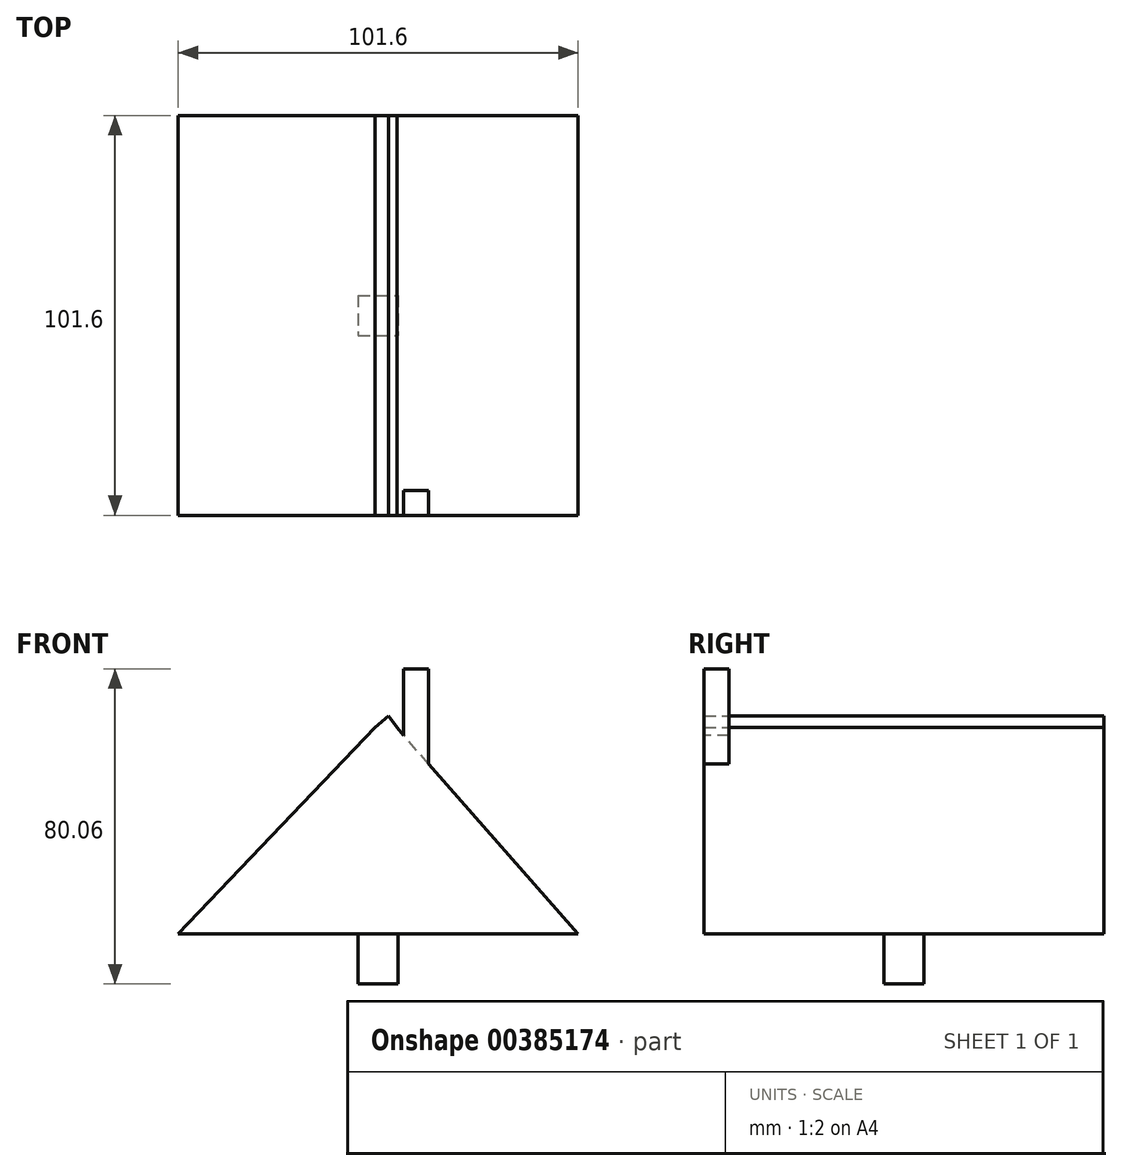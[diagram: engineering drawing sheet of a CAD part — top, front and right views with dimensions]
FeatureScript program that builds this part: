
annotation { "Feature Type Name" : "Feature", "Feature Type Description" : "" }
export const myFeature = defineFeature(function(context is Context, id is Id, definition is map)
    precondition{}
    {
        {
            var Q0;
            Q0=qCreatedBy(makeId("Front.planeOp"),FACE);
            var sketch = newSketch(context, id + "F0", { "sketchPlane" : qUnion([Q0])});
            skLineSegment(sketch, "E0", {"start": v(-53.38, -50.48) * mm, "end": v(48.22, -50.48) * mm});
            skLineSegment(sketch, "E1", {"start": v(-53.38, -50.48) * mm, "end": v(-3.4, 1.96) * mm});
            skLineSegment(sketch, "E2", {"start": v(48.22, -50.48) * mm, "end": v(2.2, 1.96) * mm});
            skLineSegment(sketch, "E3", {"start": v(-3.4, 1.96) * mm, "end": v(0, 4.94) * mm});
            skLineSegment(sketch, "E4", {"start": v(2.2, 1.96) * mm, "end": v(0, 4.94) * mm});
            skSolve(sketch);
        }
        {
            var Q0;
            Q0=makeQuery(id+"F0.imprint","IMPRINT",FACE,{"disambiguationData":[TD([[makeQuery(id+"F0.imprint","IMPRINT",EDGE,{"derivedFrom":sQuery(id+"F0.wireOp",EDGE,"E0")}),1.0]])]});
            extrude(context, id + "F1", {"entities" : qUnion([Q0]), "depth" : 101.6 * mm});
        }
        {
            var Q0;
            Q0=makeQuery(id+"F1.opExtrude","CAP_FACE",FACE,{"disambiguationData":[OSD([sQuery(id+"F0.wireOp",EDGE,"E0"),sQuery(id+"F0.wireOp",EDGE,"E1"),sQuery(id+"F0.wireOp",EDGE,"E2"),sQuery(id+"F0.wireOp",EDGE,"E3"),sQuery(id+"F0.wireOp",EDGE,"E4")])],"isStart":false});
            var sketch = newSketch(context, id + "F2", { "sketchPlane" : qUnion([Q0])});
            skLineSegment(sketch, "E5", {"start": v(3.92, 0) * mm, "end": v(3.92, 16.88) * mm});
            skLineSegment(sketch, "E6", {"start": v(3.92, 16.88) * mm, "end": v(10.27, 16.88) * mm});
            skLineSegment(sketch, "E7", {"start": v(10.27, 16.88) * mm, "end": v(10.27, -7.24) * mm});
            skSolve(sketch);
        }
        {
            var Q0;
            {var subQ0=sQuery(id+"F2.wireOp",EDGE,"E5");Q0=makeQuery(id+"F2.imprint","IMPRINT",FACE,{"disambiguationData":[TD([[makeQuery(id+"F2.imprint","IMPRINT",EDGE,{"derivedFrom":subQ0}),-1.0]])]});}
            extrude(context, id + "F3", {"entities" : qUnion([Q0]), "operationType" : NewBodyOperationType.ADD, "oppositeDirection" : true, "depth" : 6.35 * mm});
        }
        {
            var Q0;
            Q0=makeQuery(id+"F1.opExtrude","SWEPT_FACE",FACE,{"disambiguationData":[OSD([sQuery(id+"F0.wireOp",EDGE,"E0")])]});
            var sketch = newSketch(context, id + "F4", { "sketchPlane" : qUnion([Q0])});
            skLineSegment(sketch, "E8.bottom", {"start": v(2.5, 55.88) * mm, "end": v(-7.66, 55.88) * mm});
            skLineSegment(sketch, "E8.top", {"start": v(2.5, 45.72) * mm, "end": v(-7.66, 45.72) * mm});
            skLineSegment(sketch, "E8.left", {"start": v(2.5, 55.88) * mm, "end": v(2.5, 45.72) * mm});
            skLineSegment(sketch, "E8.right", {"start": v(-7.66, 55.88) * mm, "end": v(-7.66, 45.72) * mm});
            skPoint(sketch, "E8.middle", {"position": v(-2.58, 50.8) * mm});
            skSolve(sketch);
        }
        {
            var Q0;
            Q0=makeQuery(id+"F4.imprint","IMPRINT",FACE,{"disambiguationData":[TD([[makeQuery(id+"F4.imprint","IMPRINT",EDGE,{"derivedFrom":sQuery(id+"F4.wireOp",EDGE,"E8.bottom")}),1.0]])]});
            extrude(context, id + "F5", {"entities" : qUnion([Q0]), "operationType" : NewBodyOperationType.ADD, "depth" : -12.7 * mm});
        }
        {
            var Q0;
            Q0=makeQuery(id+"F1.opExtrude","SWEPT_FACE",FACE,{"disambiguationData":[OSD([sQuery(id+"F0.wireOp",EDGE,"E0")])]});
            var sketch = newSketch(context, id + "F6", { "sketchPlane" : qUnion([Q0])});
            skLineSegment(sketch, "E9.bottom", {"start": v(-7.66, 45.72) * mm, "end": v(2.5, 45.72) * mm});
            skLineSegment(sketch, "E9.top", {"start": v(-7.66, 55.88) * mm, "end": v(2.5, 55.88) * mm});
            skLineSegment(sketch, "E9.left", {"start": v(-7.66, 45.72) * mm, "end": v(-7.66, 55.88) * mm});
            skLineSegment(sketch, "E9.right", {"start": v(2.5, 45.72) * mm, "end": v(2.5, 55.88) * mm});
            skPoint(sketch, "E9.middle", {"position": v(-2.58, 50.8) * mm});
            skSolve(sketch);
        }
        {
            var Q0;
            Q0=qSketchRegion(id+"F6",true);
            extrude(context, id + "F7", {"entities" : qUnion([Q0]), "operationType" : NewBodyOperationType.ADD, "depth" : 12.7 * mm});
        }
    });
